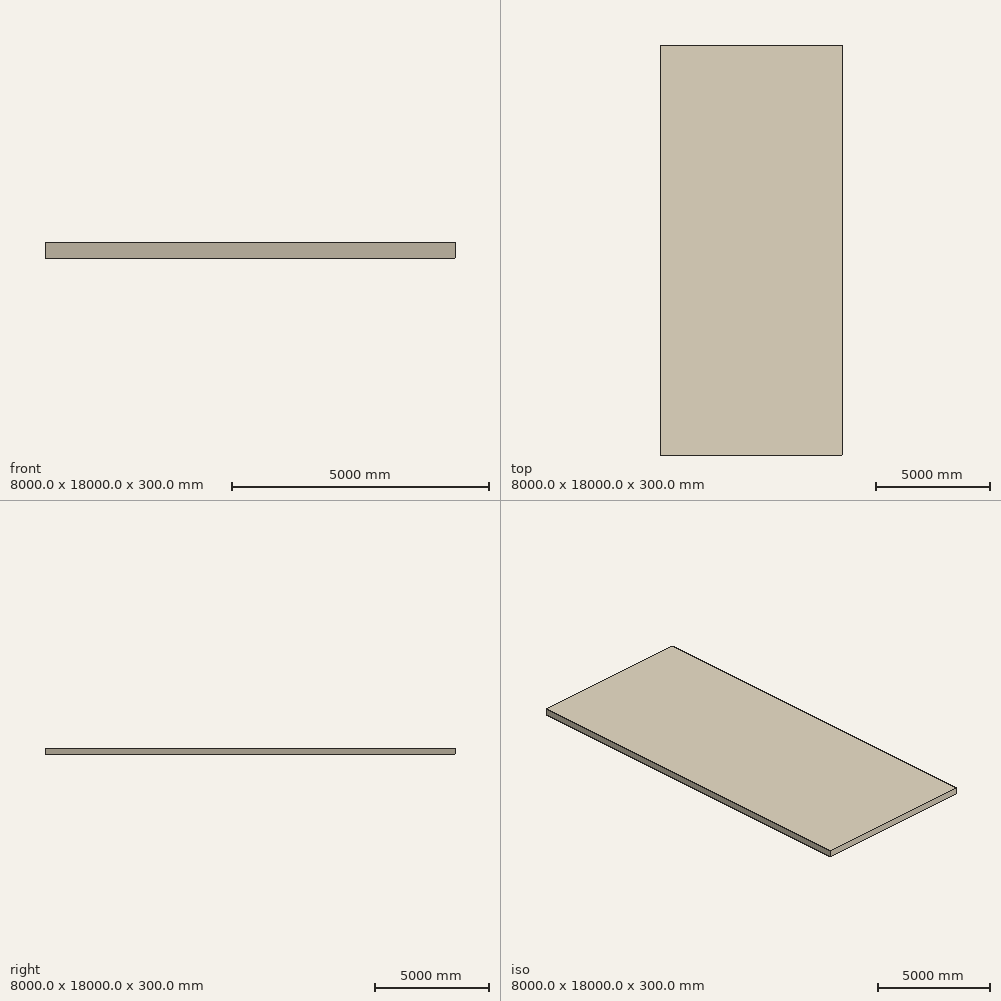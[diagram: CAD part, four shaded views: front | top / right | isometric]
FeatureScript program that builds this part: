
annotation { "Feature Type Name" : "Feature", "Feature Type Description" : "" }
export const myFeature = defineFeature(function(context is Context, id is Id, definition is map)
    precondition{}
    {
        {
            var Q0;
            Q0=qCreatedBy(makeId("Top.planeOp"),FACE);
            var sketch = newSketch(context, id + "F0", { "sketchPlane" : qUnion([Q0])});
            skLineSegment(sketch, "E0.bottom", {"start": v(-4000, 9000) * mm, "end": v(4000, 9000) * mm});
            skLineSegment(sketch, "E0.top", {"start": v(-4000, -9000) * mm, "end": v(4000, -9000) * mm});
            skLineSegment(sketch, "E0.left", {"start": v(-4000, 9000) * mm, "end": v(-4000, -9000) * mm});
            skLineSegment(sketch, "E0.right", {"start": v(4000, 9000) * mm, "end": v(4000, -9000) * mm});
            skPoint(sketch, "E0.middle", {"position": v(0, 0) * mm});
            skSolve(sketch);
        }
        {
            var Q0;
            Q0=makeQuery(id+"F0.imprint","IMPRINT",FACE,{"disambiguationData":[TD([[makeQuery(id+"F0.imprint","IMPRINT",EDGE,{"derivedFrom":sQuery(id+"F0.wireOp",EDGE,"E0.bottom")}),-1.0]])]});
            extrude(context, id + "F1", {"entities" : qUnion([Q0]), "oppositeDirection" : true, "depth" : 300 * mm, "offsetDistance" : 25 * mm});
        }
    });
